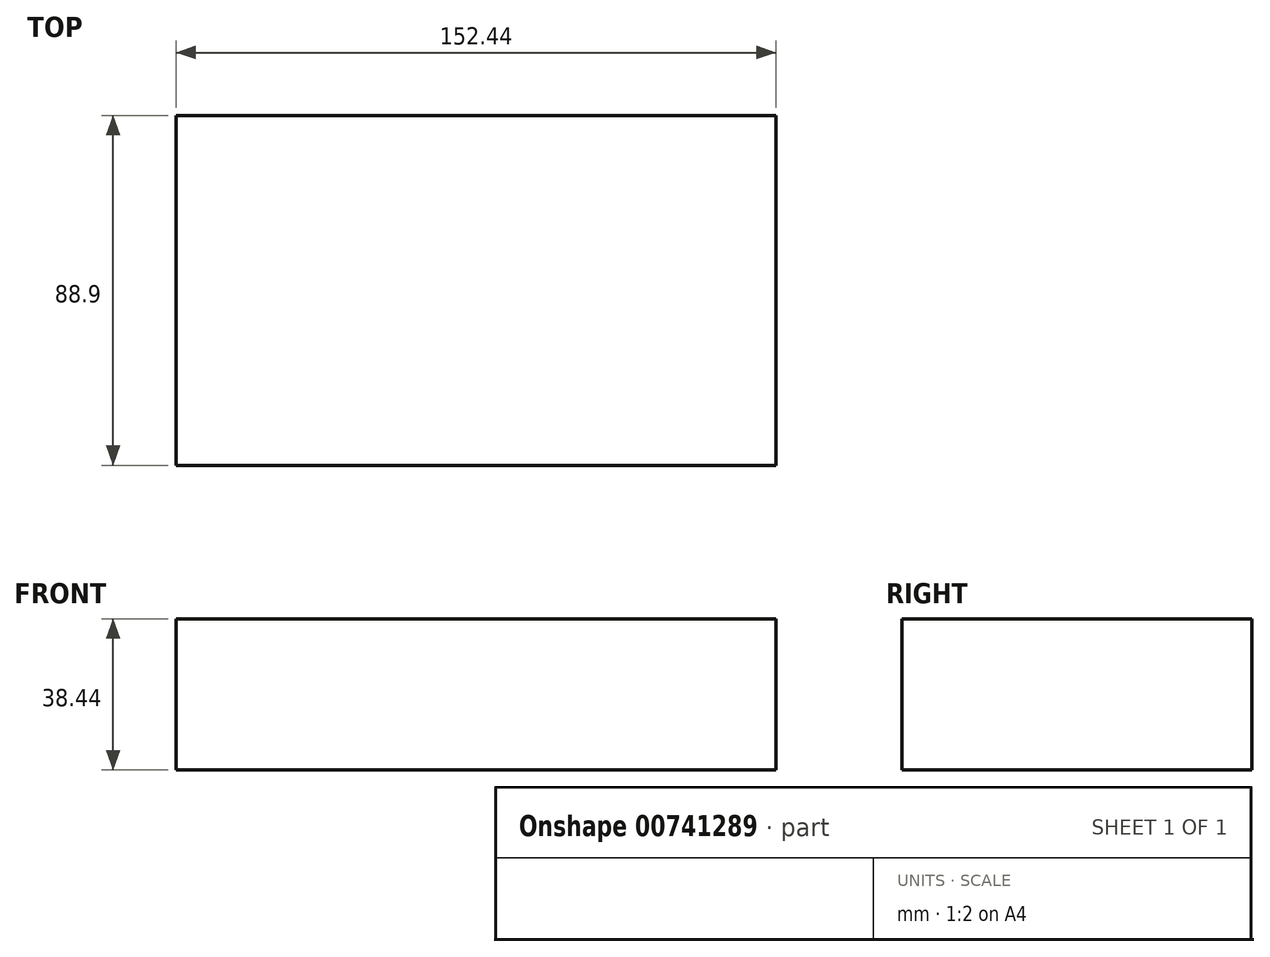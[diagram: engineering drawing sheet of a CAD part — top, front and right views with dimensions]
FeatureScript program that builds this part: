
annotation { "Feature Type Name" : "Feature", "Feature Type Description" : "" }
export const myFeature = defineFeature(function(context is Context, id is Id, definition is map)
    precondition{}
    {
        {
            var Q0;
            Q0=qCreatedBy(makeId("Front.planeOp"),FACE);
            var sketch = newSketch(context, id + "F0", { "sketchPlane" : qUnion([Q0])});
            skLineSegment(sketch, "E0.bottom", {"start": v(-76.22, 19.22) * mm, "end": v(76.22, 19.22) * mm});
            skLineSegment(sketch, "E0.top", {"start": v(-76.22, -19.22) * mm, "end": v(76.22, -19.22) * mm});
            skLineSegment(sketch, "E0.left", {"start": v(-76.22, 19.22) * mm, "end": v(-76.22, -19.22) * mm});
            skLineSegment(sketch, "E0.right", {"start": v(76.22, 19.22) * mm, "end": v(76.22, -19.22) * mm});
            skPoint(sketch, "E0.middle", {"position": v(0, 0) * mm});
            skSolve(sketch);
        }
        {
            var Q0;
            Q0=makeQuery(id+"F0.imprint","IMPRINT",FACE,{"disambiguationData":[TD([[makeQuery(id+"F0.imprint","IMPRINT",EDGE,{"derivedFrom":sQuery(id+"F0.wireOp",EDGE,"E0.bottom")}),-1.0]])]});
            extrude(context, id + "F1", {"entities" : qUnion([Q0]), "depth" : 88.9 * mm, "offsetDistance" : 25.4 * mm});
        }
    });
